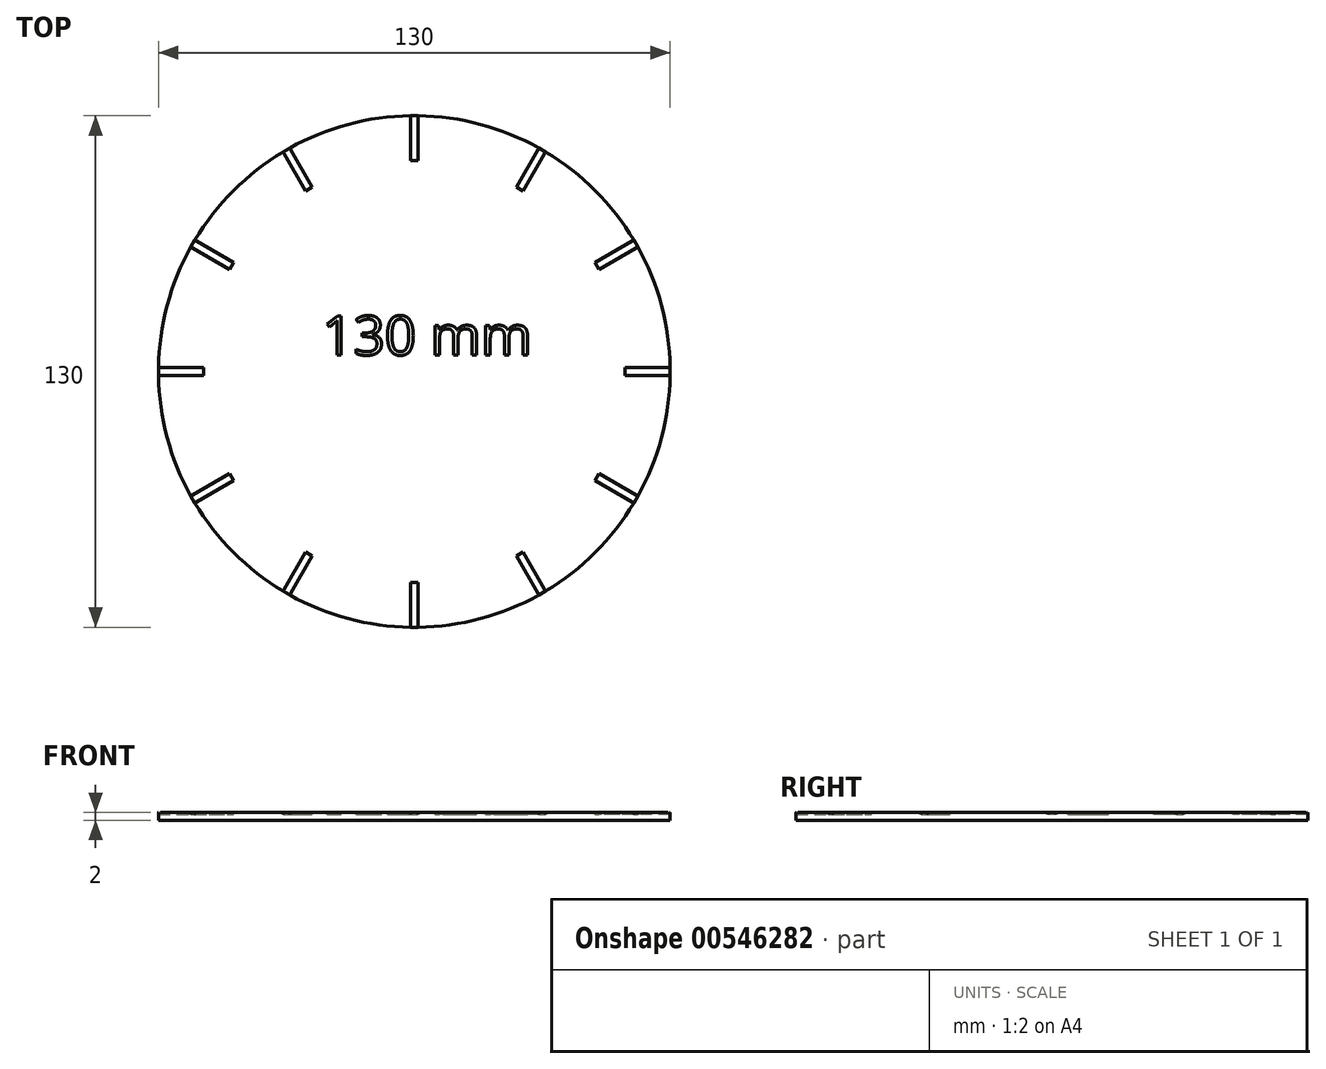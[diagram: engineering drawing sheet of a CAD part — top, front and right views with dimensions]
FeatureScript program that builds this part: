
annotation { "Feature Type Name" : "Feature", "Feature Type Description" : "" }
export const myFeature = defineFeature(function(context is Context, id is Id, definition is map)
    precondition{}
    {
        {
            var Q0;
            Q0=qCreatedBy(makeId("Top.planeOp"),FACE);
            var sketch = newSketch(context, id + "F0", { "sketchPlane" : qUnion([Q0])});
            skCircle(sketch, "E0", {"center": v(0, 0) * mm, "radius": 65 * mm});
            skSolve(sketch);
        }
        {
            var Q0;
            Q0 = qSketchRegion(id + "F0", true);
            extrude(context, id + "F1", {"entities" : qUnion([Q0]), "depth" : 2 * mm, "offsetDistance" : 25 * mm});
        }
        {
            var Q0;
            Q0=makeQuery(id+"F1.opExtrude","CAP_FACE",FACE,{"disambiguationData":[OSD([sQuery(id+"F0.wireOp",EDGE,"E0")])],"isStart":false});
            var sketch = newSketch(context, id + "F2", { "sketchPlane" : qUnion([Q0])});
            skLineSegment(sketch, "E1.bottom", {"start": v(-1, 65) * mm, "end": v(1, 65) * mm});
            skLineSegment(sketch, "E1.top", {"start": v(-1, 53.58) * mm, "end": v(1, 53.58) * mm});
            skLineSegment(sketch, "E1.left", {"start": v(-1, 65) * mm, "end": v(-1, 53.58) * mm});
            skLineSegment(sketch, "E1.right", {"start": v(1, 65) * mm, "end": v(1, 53.58) * mm});
            skLineSegment(sketch, "E2.1.0", {"start": v(-33.36, 55.78) * mm, "end": v(-27.65, 45.9) * mm});
            skLineSegment(sketch, "E2.1.1", {"start": v(-31.63, 56.78) * mm, "end": v(-25.92, 46.9) * mm});
            skLineSegment(sketch, "E2.1.2", {"start": v(-27.65, 45.9) * mm, "end": v(-25.92, 46.9) * mm});
            skLineSegment(sketch, "E2.1.3", {"start": v(-33.36, 55.78) * mm, "end": v(-31.63, 56.78) * mm});
            skLineSegment(sketch, "E2.2.0", {"start": v(-56.78, 31.63) * mm, "end": v(-46.9, 25.92) * mm});
            skLineSegment(sketch, "E2.2.1", {"start": v(-55.78, 33.36) * mm, "end": v(-45.9, 27.65) * mm});
            skLineSegment(sketch, "E2.2.2", {"start": v(-46.9, 25.92) * mm, "end": v(-45.9, 27.65) * mm});
            skLineSegment(sketch, "E2.2.3", {"start": v(-56.78, 31.63) * mm, "end": v(-55.78, 33.36) * mm});
            skPoint(sketch, "E2.center", {"position": v(0, 0) * mm});
            skLineSegment(sketch, "E3.2.3.0", {"start": v(-65, -1) * mm, "end": v(-53.58, -1) * mm});
            skLineSegment(sketch, "E3.3.3.0", {"start": v(-65, 1) * mm, "end": v(-53.58, 1) * mm});
            skLineSegment(sketch, "E3.6.3.0", {"start": v(-53.58, -1) * mm, "end": v(-53.58, 1) * mm});
            skLineSegment(sketch, "E3.9.3.0", {"start": v(-65, -1) * mm, "end": v(-65, 1) * mm});
            skLineSegment(sketch, "E3.2.4.0", {"start": v(-55.78, -33.36) * mm, "end": v(-45.9, -27.65) * mm});
            skLineSegment(sketch, "E3.3.4.0", {"start": v(-56.78, -31.63) * mm, "end": v(-46.9, -25.92) * mm});
            skLineSegment(sketch, "E3.6.4.0", {"start": v(-45.9, -27.65) * mm, "end": v(-46.9, -25.92) * mm});
            skLineSegment(sketch, "E3.9.4.0", {"start": v(-55.78, -33.36) * mm, "end": v(-56.78, -31.63) * mm});
            skLineSegment(sketch, "E3.2.5.0", {"start": v(-31.63, -56.78) * mm, "end": v(-25.92, -46.9) * mm});
            skLineSegment(sketch, "E3.3.5.0", {"start": v(-33.36, -55.78) * mm, "end": v(-27.65, -45.9) * mm});
            skLineSegment(sketch, "E3.6.5.0", {"start": v(-25.92, -46.9) * mm, "end": v(-27.65, -45.9) * mm});
            skLineSegment(sketch, "E3.9.5.0", {"start": v(-31.63, -56.78) * mm, "end": v(-33.36, -55.78) * mm});
            skLineSegment(sketch, "E3.2.6.0", {"start": v(1, -65) * mm, "end": v(1, -53.58) * mm});
            skLineSegment(sketch, "E3.3.6.0", {"start": v(-1, -65) * mm, "end": v(-1, -53.58) * mm});
            skLineSegment(sketch, "E3.6.6.0", {"start": v(1, -53.58) * mm, "end": v(-1, -53.58) * mm});
            skLineSegment(sketch, "E3.9.6.0", {"start": v(1, -65) * mm, "end": v(-1, -65) * mm});
            skLineSegment(sketch, "E3.2.7.0", {"start": v(33.36, -55.78) * mm, "end": v(27.65, -45.9) * mm});
            skLineSegment(sketch, "E3.3.7.0", {"start": v(31.63, -56.78) * mm, "end": v(25.92, -46.9) * mm});
            skLineSegment(sketch, "E3.6.7.0", {"start": v(27.65, -45.9) * mm, "end": v(25.92, -46.9) * mm});
            skLineSegment(sketch, "E3.9.7.0", {"start": v(33.36, -55.78) * mm, "end": v(31.63, -56.78) * mm});
            skLineSegment(sketch, "E3.2.8.0", {"start": v(56.78, -31.63) * mm, "end": v(46.9, -25.92) * mm});
            skLineSegment(sketch, "E3.3.8.0", {"start": v(55.78, -33.36) * mm, "end": v(45.9, -27.65) * mm});
            skLineSegment(sketch, "E3.6.8.0", {"start": v(46.9, -25.92) * mm, "end": v(45.9, -27.65) * mm});
            skLineSegment(sketch, "E3.9.8.0", {"start": v(56.78, -31.63) * mm, "end": v(55.78, -33.36) * mm});
            skLineSegment(sketch, "E3.2.9.0", {"start": v(65, 1) * mm, "end": v(53.58, 1) * mm});
            skLineSegment(sketch, "E3.3.9.0", {"start": v(65, -1) * mm, "end": v(53.58, -1) * mm});
            skLineSegment(sketch, "E3.6.9.0", {"start": v(53.58, 1) * mm, "end": v(53.58, -1) * mm});
            skLineSegment(sketch, "E3.9.9.0", {"start": v(65, 1) * mm, "end": v(65, -1) * mm});
            skLineSegment(sketch, "E3.2.10.0", {"start": v(55.78, 33.36) * mm, "end": v(45.9, 27.65) * mm});
            skLineSegment(sketch, "E3.3.10.0", {"start": v(56.78, 31.63) * mm, "end": v(46.9, 25.92) * mm});
            skLineSegment(sketch, "E3.6.10.0", {"start": v(45.9, 27.65) * mm, "end": v(46.9, 25.92) * mm});
            skLineSegment(sketch, "E3.9.10.0", {"start": v(55.78, 33.36) * mm, "end": v(56.78, 31.63) * mm});
            skLineSegment(sketch, "E3.2.11.0", {"start": v(31.63, 56.78) * mm, "end": v(25.92, 46.9) * mm});
            skLineSegment(sketch, "E3.3.11.0", {"start": v(33.36, 55.78) * mm, "end": v(27.65, 45.9) * mm});
            skLineSegment(sketch, "E3.6.11.0", {"start": v(25.92, 46.9) * mm, "end": v(27.65, 45.9) * mm});
            skLineSegment(sketch, "E3.9.11.0", {"start": v(31.63, 56.78) * mm, "end": v(33.36, 55.78) * mm});
            skSolve(sketch);
        }
        {
            var Q0;
            Q0 = qSketchRegion(id + "F2", true);
            extrude(context, id + "F3", {"entities" : qUnion([Q0]), "operationType" : NewBodyOperationType.REMOVE, "oppositeDirection" : true, "depth" : 0.5 * mm, "offsetDistance" : 25 * mm});
        }
        {
            var Q0;
            Q0=makeQuery(id+"F1.opExtrude","CAP_FACE",FACE,{"disambiguationData":[OSD([sQuery(id+"F0.wireOp",EDGE,"E0")])],"isStart":false});
            var sketch = newSketch(context, id + "F4", { "sketchPlane" : qUnion([Q0])});
            skText(sketch, "E4", { "text": "130 mm\n", "fontName": "OpenSans-Regular.ttf"});
            const initialGuessF4  = {"E4": [-0.0234, 0.0042, 1, 0, 0.01]};
            skSetInitialGuess(sketch, initialGuessF4);
            skSolve(sketch);
        }
        {
            var Q0;
            Q0 = qSketchRegion(id + "F4", true);
            extrude(context, id + "F5", {"entities" : qUnion([Q0]), "operationType" : NewBodyOperationType.REMOVE, "oppositeDirection" : true, "depth" : 0.5 * mm, "offsetDistance" : 25 * mm});
        }
        {
            var Q0;
            {var subQ0=sQuery(id+"F0.wireOp",EDGE,"E0");Q0=makeQuery(id+"F3.boolean.opBoolean","SPLIT",EDGE,{"disambiguationData":[TD([makeQuery(id+"F3.opExtrude","SWEPT_FACE",FACE,{"disambiguationData":[OSD([sQuery(id+"F2.wireOp",EDGE,"E3.2.6.0")])]})])],"derivedFrom":makeQuery(id+"F1.opExtrude","CAP_EDGE",EDGE,{"disambiguationData":[OSD([subQ0])],"isStart":false})});}
            var Q1;
            {var subQ0=sQuery(id+"F0.wireOp",EDGE,"E0");Q1=makeQuery(id+"F3.boolean.opBoolean","SPLIT",EDGE,{"disambiguationData":[TD([makeQuery(id+"F3.opExtrude","SWEPT_FACE",FACE,{"disambiguationData":[OSD([sQuery(id+"F2.wireOp",EDGE,"E3.2.5.0")])]})])],"derivedFrom":makeQuery(id+"F1.opExtrude","CAP_EDGE",EDGE,{"disambiguationData":[OSD([subQ0])],"isStart":false})});}
            var Q2;
            {var subQ0=sQuery(id+"F0.wireOp",EDGE,"E0");Q2=makeQuery(id+"F3.boolean.opBoolean","SPLIT",EDGE,{"disambiguationData":[TD([makeQuery(id+"F3.opExtrude","SWEPT_FACE",FACE,{"disambiguationData":[OSD([sQuery(id+"F2.wireOp",EDGE,"E3.2.4.0")])]})])],"derivedFrom":makeQuery(id+"F1.opExtrude","CAP_EDGE",EDGE,{"disambiguationData":[OSD([subQ0])],"isStart":false})});}
            var Q3;
            {var subQ0=sQuery(id+"F0.wireOp",EDGE,"E0");Q3=makeQuery(id+"F3.boolean.opBoolean","SPLIT",EDGE,{"disambiguationData":[TD([makeQuery(id+"F3.opExtrude","SWEPT_FACE",FACE,{"disambiguationData":[OSD([sQuery(id+"F2.wireOp",EDGE,"E3.2.3.0")])]})])],"derivedFrom":makeQuery(id+"F1.opExtrude","CAP_EDGE",EDGE,{"disambiguationData":[OSD([subQ0])],"isStart":false})});}
            var Q4;
            {var subQ0=sQuery(id+"F0.wireOp",EDGE,"E0");Q4=makeQuery(id+"F3.boolean.opBoolean","SPLIT",EDGE,{"disambiguationData":[TD([makeQuery(id+"F3.opExtrude","SWEPT_FACE",FACE,{"disambiguationData":[OSD([sQuery(id+"F2.wireOp",EDGE,"E2.2.0")])]})])],"derivedFrom":makeQuery(id+"F1.opExtrude","CAP_EDGE",EDGE,{"disambiguationData":[OSD([subQ0])],"isStart":false})});}
            var Q5;
            {var subQ0=sQuery(id+"F0.wireOp",EDGE,"E0");Q5=makeQuery(id+"F3.boolean.opBoolean","SPLIT",EDGE,{"disambiguationData":[TD([makeQuery(id+"F3.opExtrude","SWEPT_FACE",FACE,{"disambiguationData":[OSD([sQuery(id+"F2.wireOp",EDGE,"E3.2.7.0")])]})])],"derivedFrom":makeQuery(id+"F1.opExtrude","CAP_EDGE",EDGE,{"disambiguationData":[OSD([subQ0])],"isStart":false})});}
            var Q6;
            {var subQ0=sQuery(id+"F0.wireOp",EDGE,"E0");Q6=makeQuery(id+"F3.boolean.opBoolean","SPLIT",EDGE,{"disambiguationData":[TD([makeQuery(id+"F3.opExtrude","SWEPT_FACE",FACE,{"disambiguationData":[OSD([sQuery(id+"F2.wireOp",EDGE,"E3.2.8.0")])]})])],"derivedFrom":makeQuery(id+"F1.opExtrude","CAP_EDGE",EDGE,{"disambiguationData":[OSD([subQ0])],"isStart":false})});}
            var Q7;
            {var subQ0=sQuery(id+"F0.wireOp",EDGE,"E0");Q7=makeQuery(id+"F3.boolean.opBoolean","SPLIT",EDGE,{"disambiguationData":[TD([makeQuery(id+"F3.opExtrude","SWEPT_FACE",FACE,{"disambiguationData":[OSD([sQuery(id+"F2.wireOp",EDGE,"E3.2.9.0")])]})])],"derivedFrom":makeQuery(id+"F1.opExtrude","CAP_EDGE",EDGE,{"disambiguationData":[OSD([subQ0])],"isStart":false})});}
            var Q8;
            {var subQ0=sQuery(id+"F0.wireOp",EDGE,"E0");Q8=makeQuery(id+"F3.boolean.opBoolean","SPLIT",EDGE,{"disambiguationData":[TD([makeQuery(id+"F3.opExtrude","SWEPT_FACE",FACE,{"disambiguationData":[OSD([sQuery(id+"F2.wireOp",EDGE,"E3.2.10.0")])]})])],"derivedFrom":makeQuery(id+"F1.opExtrude","CAP_EDGE",EDGE,{"disambiguationData":[OSD([subQ0])],"isStart":false})});}
            var Q9;
            {var subQ0=sQuery(id+"F0.wireOp",EDGE,"E0");Q9=makeQuery(id+"F3.boolean.opBoolean","SPLIT",EDGE,{"disambiguationData":[TD([makeQuery(id+"F3.opExtrude","SWEPT_FACE",FACE,{"disambiguationData":[OSD([sQuery(id+"F2.wireOp",EDGE,"E1.right")])]})])],"derivedFrom":makeQuery(id+"F1.opExtrude","CAP_EDGE",EDGE,{"disambiguationData":[OSD([subQ0])],"isStart":false})});}
            var Q10;
            {var subQ0=sQuery(id+"F0.wireOp",EDGE,"E0");Q10=makeQuery(id+"F3.boolean.opBoolean","SPLIT",EDGE,{"disambiguationData":[TD([makeQuery(id+"F3.opExtrude","SWEPT_FACE",FACE,{"disambiguationData":[OSD([sQuery(id+"F2.wireOp",EDGE,"E1.left")])]})])],"derivedFrom":makeQuery(id+"F1.opExtrude","CAP_EDGE",EDGE,{"disambiguationData":[OSD([subQ0])],"isStart":false})});}
            var Q11;
            {var subQ0=sQuery(id+"F0.wireOp",EDGE,"E0");Q11=makeQuery(id+"F3.boolean.opBoolean","SPLIT",EDGE,{"disambiguationData":[TD([makeQuery(id+"F3.opExtrude","SWEPT_FACE",FACE,{"disambiguationData":[OSD([sQuery(id+"F2.wireOp",EDGE,"E2.1.0")])]})])],"derivedFrom":makeQuery(id+"F1.opExtrude","CAP_EDGE",EDGE,{"disambiguationData":[OSD([subQ0])],"isStart":false})});}
            fillet(context, id + "F6", {"entities" : qUnion([Q0, Q1, Q2, Q3, Q4, Q5, Q6, Q7, Q8, Q9, Q10, Q11]), "radius" : .5 * mm, "tangentPropagation" : true, "allowEdgeOverflow" : false});
        }
    });
